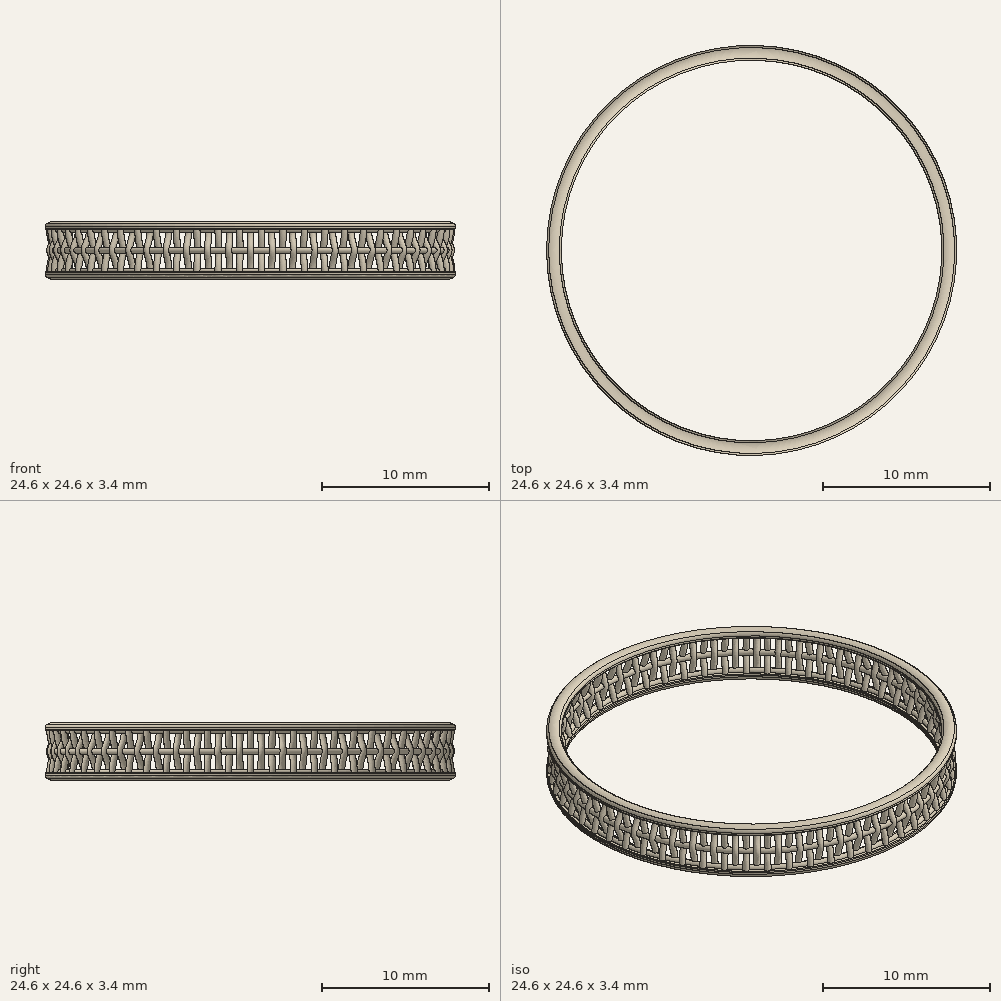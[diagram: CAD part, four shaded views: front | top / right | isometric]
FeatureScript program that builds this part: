
annotation { "Feature Type Name" : "Feature", "Feature Type Description" : "" }
export const myFeature = defineFeature(function(context is Context, id is Id, definition is map)
    precondition{}
    {
        {
            var Q0;
            Q0=qCreatedBy(makeId("Top.planeOp"),FACE);
            var sketch = newSketch(context, id + "F0", { "sketchPlane" : qUnion([Q0])});
            skCircle(sketch, "E0", {"center": v(0, 0) * mm, "radius": 12.07 * mm});
            skSolve(sketch);
        }
        {
            var Q0;
            Q0=qCreatedBy(makeId("Front.planeOp"),FACE);
            var sketch = newSketch(context, id + "F1", { "sketchPlane" : qUnion([Q0])});
            skFitSpline(sketch, "E1", {"points": [v(12.07, 1.27) * mm, v(11.81, 0) * mm, v(12.07, -1.27) * mm], "startDerivative": vector(0, -3.81) * mm, "endDerivative": vector(0, -3.81) * mm});
            skLineSegment(sketch, "E2", {"start": v(12.07, 1.27) * mm, "end": v(12.07, -1.27) * mm, "construction": true});
            skSolve(sketch);
        }
        {
            var Q0;
            Q0=qCreatedBy(makeId("Top.planeOp"),FACE);
            cPlane(context, id + "F2", {"entities" : qUnion([Q0]), "cplaneType" : CPlaneType.OFFSET, "offset" : 1.27 * mm, "oppositeDirection" : true, "width" : 152.4 * mm, "height" : 152.4 * mm});
        }
        {
            var Q0;
            Q0=qCreatedBy(id+"F2.planeOp",FACE);
            var sketch = newSketch(context, id + "F3", { "sketchPlane" : qUnion([Q0])});
            skCircle(sketch, "E3", {"center": v(12.07, 0) * mm, "radius": 0.2 * mm});
            skSolve(sketch);
        }
        {
            var Q0;
            Q0=makeQuery(id+"F3.imprint","IMPRINT",FACE,{"disambiguationData":[TD([[makeQuery(id+"F3.imprint","IMPRINT",EDGE,{"derivedFrom":sQuery(id+"F3.wireOp",EDGE,"E3")}),1.0]])]});
            var Q1;
            Q1=sQuery(id+"F1.wireOp",EDGE,"E1");
            sweep(context, id + "F4", {"profiles" : qUnion([Q0]), "path" : qUnion([Q1])});
        }
        {
            var Q0;
            Q0=qCreatedBy(makeId("Right.planeOp"),FACE);
            var sketch = newSketch(context, id + "F5", { "sketchPlane" : qUnion([Q0])});
            skLineSegment(sketch, "E4", {"start": v(-12.07, 1.27) * mm, "end": v(-12.07, -1.27) * mm, "construction": true});
            skFitSpline(sketch, "E5", {"points": [v(-11.68, 1.27) * mm, v(-12.07, 0) * mm, v(-11.68, -1.27) * mm], "startDerivative": vector(-0.03, -3.81) * mm, "endDerivative": vector(0.03, -3.81) * mm});
            skLineSegment(sketch, "E6", {"start": v(-12.07, -1.27) * mm, "end": v(-11.68, -1.27) * mm, "construction": true});
            skLineSegment(sketch, "E7", {"start": v(-12.07, 1.27) * mm, "end": v(-11.68, 1.27) * mm, "construction": true});
            skSolve(sketch);
        }
        {
            var Q0;
            Q0=qCreatedBy(id+"F2.planeOp",FACE);
            var sketch = newSketch(context, id + "F6", { "sketchPlane" : qUnion([Q0])});
            skCircle(sketch, "E8", {"center": v(0, -11.68) * mm, "radius": 0.2 * mm});
            skSolve(sketch);
        }
        {
            var Q0;
            Q0=makeQuery(id+"F6.imprint","IMPRINT",FACE,{"disambiguationData":[TD([[makeQuery(id+"F6.imprint","IMPRINT",EDGE,{"derivedFrom":sQuery(id+"F6.wireOp",EDGE,"E8")}),1.0]])]});
            var Q1;
            Q1=sQuery(id+"F5.wireOp",EDGE,"E5");
            sweep(context, id + "F7", {"profiles" : qUnion([Q0]), "path" : qUnion([Q1])});
        }
        {
            var Q0;
            Q0=qCreatedBy(makeId("Front.planeOp"),FACE);
            var sketch = newSketch(context, id + "F8", { "sketchPlane" : qUnion([Q0])});
            skLineSegment(sketch, "E9", {"start": v(0, 0) * mm, "end": v(0, -7.15) * mm, "construction": true});
            skSolve(sketch);
        }
        {
            var Q0;
            Q0=makeQuery(id+"F7.opSweep","SWEPT_BODY",BODY,{"disambiguationData":[OSD([sQuery(id+"F5.wireOp",EDGE,"E5"),sQuery(id+"F6.wireOp",EDGE,"E8")])]});
            var Q1;
            Q1=sQuery(id+"F8.wireOp",EDGE,"E9");
            circularPattern(context, id + "F9", {"entities" : qUnion([Q0]), "axis" : qUnion([Q1]), "angle" : 360 * degree, "instanceCount" : 58, "equalSpace" : true});
        }
        {
            var Q0;
            Q0=makeQuery(id+"F4.opSweep","SWEPT_BODY",BODY,{"disambiguationData":[OSD([sQuery(id+"F1.wireOp",EDGE,"E1"),sQuery(id+"F3.wireOp",EDGE,"E3")])]});
            var Q1;
            Q1=sQuery(id+"F8.wireOp",EDGE,"E9");
            circularPattern(context, id + "F10", {"entities" : qUnion([Q0]), "axis" : qUnion([Q1]), "angle" : 360 * degree, "instanceCount" : 58, "equalSpace" : true});
        }
        {
            var Q0;
            Q0=qCreatedBy(makeId("Right.planeOp"),FACE);
            var sketch = newSketch(context, id + "F11", { "sketchPlane" : qUnion([Q0])});
            skCircle(sketch, "E10", {"center": v(-11.94, 0) * mm, "radius": 0.2 * mm});
            skSolve(sketch);
        }
        {
            var Q0;
            Q0=makeQuery(id+"F11.imprint","IMPRINT",FACE,{"disambiguationData":[TD([[makeQuery(id+"F11.imprint","IMPRINT",EDGE,{"derivedFrom":sQuery(id+"F11.wireOp",EDGE,"E10")}),1.0]])]});
            var Q1;
            Q1=sQuery(id+"F8.wireOp",EDGE,"E9");
            revolve(context, id + "F12", {"surfaceOperationType" : NewSurfaceOperationType.NEW, "entities" : qUnion([Q0]), "axis" : qUnion([Q1]), "revolveType" : RevolveType.FULL});
        }
        {
            var Q0;
            Q0=qCreatedBy(makeId("Right.planeOp"),FACE);
            var sketch = newSketch(context, id + "F13", { "sketchPlane" : qUnion([Q0])});
            skLineSegment(sketch, "E11.top", {"start": v(-12.32, 1.24) * mm, "end": v(-12.07, 1.24) * mm});
            skLineSegment(sketch, "E11.left", {"start": v(-12.32, 1.54) * mm, "end": v(-12.32, 1.24) * mm});
            skLineSegment(sketch, "E11.right", {"start": v(-11.43, 1.54) * mm, "end": v(-11.43, 1.24) * mm});
            skArc(sketch, "E12", {"start": v(-12.07, 1.24) * mm, "mid": v(-11.87, 1.05) * mm, "end": v(-11.68, 1.24) * mm});
            skLineSegment(sketch, "E13.trimOffspring", {"start": v(-11.68, 1.24) * mm, "end": v(-11.43, 1.24) * mm});
            skLineSegment(sketch, "E14.MirrorCS", {"start": v(-11.68, -1.24) * mm, "end": v(-11.43, -1.24) * mm});
            skArc(sketch, "E15.MirrorCS", {"start": v(-12.07, -1.24) * mm, "mid": v(-11.87, -1.05) * mm, "end": v(-11.68, -1.24) * mm});
            skLineSegment(sketch, "E16.MirrorCS", {"start": v(-11.43, -1.54) * mm, "end": v(-11.43, -1.24) * mm});
            skLineSegment(sketch, "E17.MirrorCS", {"start": v(-12.32, -1.24) * mm, "end": v(-12.06, -1.24) * mm});
            skLineSegment(sketch, "E18.MirrorCS", {"start": v(-12.32, -1.54) * mm, "end": v(-12.32, -1.24) * mm});
            skArc(sketch, "E19", {"start": v(-11.43, 1.54) * mm, "mid": v(-11.87, 1.72) * mm, "end": v(-12.32, 1.54) * mm});
            skArc(sketch, "E20", {"start": v(-12.32, -1.54) * mm, "mid": v(-11.87, -1.72) * mm, "end": v(-11.43, -1.54) * mm});
            skSolve(sketch);
        }
        {
            var Q0;
            Q0=makeQuery(id+"F13.imprint","IMPRINT",FACE,{"disambiguationData":[TD([[makeQuery(id+"F13.imprint","IMPRINT",EDGE,{"derivedFrom":sQuery(id+"F13.wireOp",EDGE,"E11.top")}),1.0]])]});
            var Q1;
            Q1=makeQuery(id+"F13.imprint","IMPRINT",FACE,{"disambiguationData":[TD([[makeQuery(id+"F13.imprint","IMPRINT",EDGE,{"derivedFrom":sQuery(id+"F13.wireOp",EDGE,"E14.MirrorCS")}),-1.0]])]});
            var Q2;
            Q2=sQuery(id+"F8.wireOp",EDGE,"E9");
            revolve(context, id + "F14", {"surfaceOperationType" : NewSurfaceOperationType.NEW, "entities" : qUnion([Q0, Q1]), "axis" : qUnion([Q2]), "revolveType" : RevolveType.FULL});
        }
        {
            var Q0;
            Q0=makeQuery(id+"F14.opRevolve","SWEPT_EDGE",EDGE,{"disambiguationData":[OSD([sQuery(id+"F13.wireOp",EDGE,"E11.left"),sQuery(id+"F13.wireOp",EDGE,"E19")])]});
            var Q1;
            Q1=makeQuery(id+"F14.opRevolve","SWEPT_FACE",FACE,{"disambiguationData":[OSD([sQuery(id+"F13.wireOp",EDGE,"E19")])]});
            var Q2;
            Q2=makeQuery(id+"F14.opRevolve","SWEPT_EDGE",EDGE,{"disambiguationData":[OSD([sQuery(id+"F13.wireOp",EDGE,"E18.MirrorCS"),sQuery(id+"F13.wireOp",EDGE,"E20")])]});
            var Q3;
            Q3=makeQuery(id+"F14.opRevolve","SWEPT_EDGE",EDGE,{"disambiguationData":[OSD([sQuery(id+"F13.wireOp",EDGE,"E16.MirrorCS"),sQuery(id+"F13.wireOp",EDGE,"E20")])]});
            fillet(context, id + "F15", {"entities" : qUnion([Q0, Q1, Q2, Q3]), "radius" : 0.25 * mm, "tangentPropagation" : true, "allowEdgeOverflow" : false});
        }
        {
            var Q0;
            Q0=makeQuery(id+"F14.opRevolve","SWEPT_EDGE",EDGE,{"disambiguationData":[OSD([sQuery(id+"F13.wireOp",EDGE,"E17.MirrorCS"),sQuery(id+"F13.wireOp",EDGE,"E18.MirrorCS")])]});
            var Q1;
            Q1=makeQuery(id+"F14.opRevolve","SWEPT_EDGE",EDGE,{"disambiguationData":[OSD([sQuery(id+"F13.wireOp",EDGE,"E11.top"),sQuery(id+"F13.wireOp",EDGE,"E11.left")])]});
            var Q2;
            Q2=makeQuery(id+"F14.opRevolve","SWEPT_EDGE",EDGE,{"disambiguationData":[OSD([sQuery(id+"F13.wireOp",EDGE,"E11.right"),sQuery(id+"F13.wireOp",EDGE,"E13.trimOffspring")])]});
            var Q3;
            Q3=makeQuery(id+"F14.opRevolve","SWEPT_EDGE",EDGE,{"disambiguationData":[OSD([sQuery(id+"F13.wireOp",EDGE,"E14.MirrorCS"),sQuery(id+"F13.wireOp",EDGE,"E16.MirrorCS")])]});
            fillet(context, id + "F16", {"entities" : qUnion([Q0, Q1, Q2, Q3]), "radius" : 0.05 * mm, "tangentPropagation" : true, "allowEdgeOverflow" : false});
        }
    });
